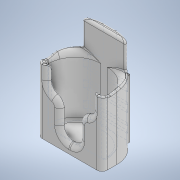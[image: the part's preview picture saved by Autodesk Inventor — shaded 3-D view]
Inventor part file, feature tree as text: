
AUTODESK INVENTOR PART (.ipt)
format: ipt  version: 2022 (Build 260153000, 153)  size: 602,624 bytes
history: native  units: in
note: dims shown in document units (in); Inventor stores cm internally (conversion verified against a paired STEP export)
features: fillet x9, extrude x7, sketch x7
ambient origin geometry x8: Origin, YZ Plane, XZ Plane, XY Plane, X Axis, Y Axis, Z Axis, Center Point
bodies: Solid1 (feature_tree)
feature tree (23):
  extrude  "Extrusion1"  Depth=2.7559in
  extrude  "Extrusion2"  Depth=1.9685in
  extrude  "Extrusion3"  Depth=0.8858in
  extrude  "Extrusion4"  Depth=0.0984in
  fillet  "Fillet1"  Radius=0.0984in
  fillet  "Fillet2"  Radius=1.811in
  extrude  "Extrusion5"  Depth=1.378in
  fillet  "Fillet3"  Radius=0.2953in
  fillet  "Fillet4"  Radius=0.2953in
  fillet  "Fillet5"  Radius=0.1575in
  fillet  "Fillet6"  Radius=0.0787in
  fillet  "Fillet7"  Radius=0.7874in
  extrude  "Extrusion6"  Depth=0.689in
  extrude  "Extrusion7"  Depth=0.1575in TaperAngle=0.0deg
  fillet  "Fillet8"  Radius=0.9843in
  fillet  "Fillet9"  Radius=0.2756in
  sketch  "Sketch1"  dims[d0=1.9685in d1=2.7559in]
  sketch  "Sketch2"  dims[d2=0.1969in d3=0.0in d4=1.9685in]
  sketch  "Sketch3"  dims[d5=1.0433in d6=0.0in d7=0.8858in]
  sketch  "Sketch4"  dims[d8=1.7717in d9=0.0984in d10=0.0984in d11=1.811in d12=0.0in]
  sketch  "Sketch5"  dims[d13=1.1024in d14=1.378in d15=0.2953in d16=0.2953in d17=0.1575in d18=0.0in d19=0.0787in d20=0.7874in]
  sketch  "Sketch6"  dims[d21=0.5906in d22=0.689in]
  sketch  "Sketch7"  dims[d23=0.689in d24=0.1575in d25=0.0in d26=0.9843in d27=0.2756in d28=0.1575in d29=0.0394in d30=0.7874in d31=0.0787in d32=0.3937in d33=0.3937in d34=0.0in d35=0.1969in d36=0.1181in d37=0.0in d38=0.1969in d39=0.1969in d40=0.1969in d41=0.0787in d42=0.0787in d43=0.3445in d44=0.3445in d45=0.3445in d46=0.3445in d47=0.0in d48=0.0in d49=0.0394in d50=0.0197in]
